# Revit family: TubReplacement_ProSlope_NobleCompany
name_source: partatom
category: Specialty Equipment
revit_build: Autodesk Revit 2016 (Build: 20150714_1515(x64)
units: mm (PartAtom-declared; Revit-internal decimal feet)

## family parameters
Cut with Voids When Loaded = No
Host = Face
OmniClass Number = 23.45.55.21
OmniClass Title = Drains (Wastes)
Part Type = Normal
Room Calculation Point = No
Round Connector Dimension = Use Diameter
Shared = No

## types (2) — shared parameters
Assembly Code = D2030300
Base = Polymer coated Expanded Polystyrene
Building Codes = http://www.noblecompany.com
Default Elevation = 0"
Depth = 40"
Description = Noble Pro Slope 4080 Tub Replacement
Drain Hole Diameter = 3"
Hang = 1/8"
Height = 1"
Installation-Fabrication = http://www.noblecompany.com
Manufacturer = Noble Company
Manufacturer Fax = 231-799-8850
Model = Pro Slope 4080 Tub Replacement
Panel Size = 16"
Product Data = http://www.noblecompany.com
Product Properties = http://www.noblecompany.com
URL = www.noblecompany.com
Width = 80"

## per-type parameters (varying)
| type | Extension Type |
| 40x80 - Tapered Extension | ShowerBase_ProSlopeExtension_NobleCompany : 20x40 Tapered |
| 40x80 - Flat Extension | ShowerBase_ProSlopeExtension_NobleCompany : 20x40 Flat |

## geometry (parser evidence)
native form markers: Sweep x5
no freeform markers — native parametric forms only
